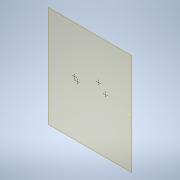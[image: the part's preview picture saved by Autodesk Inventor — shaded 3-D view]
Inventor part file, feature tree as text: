
AUTODESK INVENTOR PART (.ipt)
format: ipt  version: 2021 (Build 250183000, 183)  size: 84,480 bytes
history: native  units: in
note: dims shown in document units (in); Inventor stores cm internally (conversion verified against a paired STEP export)
features: plane x1, sketch x1
ambient origin geometry x8: Origin, YZ Plane, XZ Plane, XY Plane, X Axis, Y Axis, Z Axis, Center Point
feature tree (2):
  plane  "Work Plane1"
  sketch  "Sketch1"
